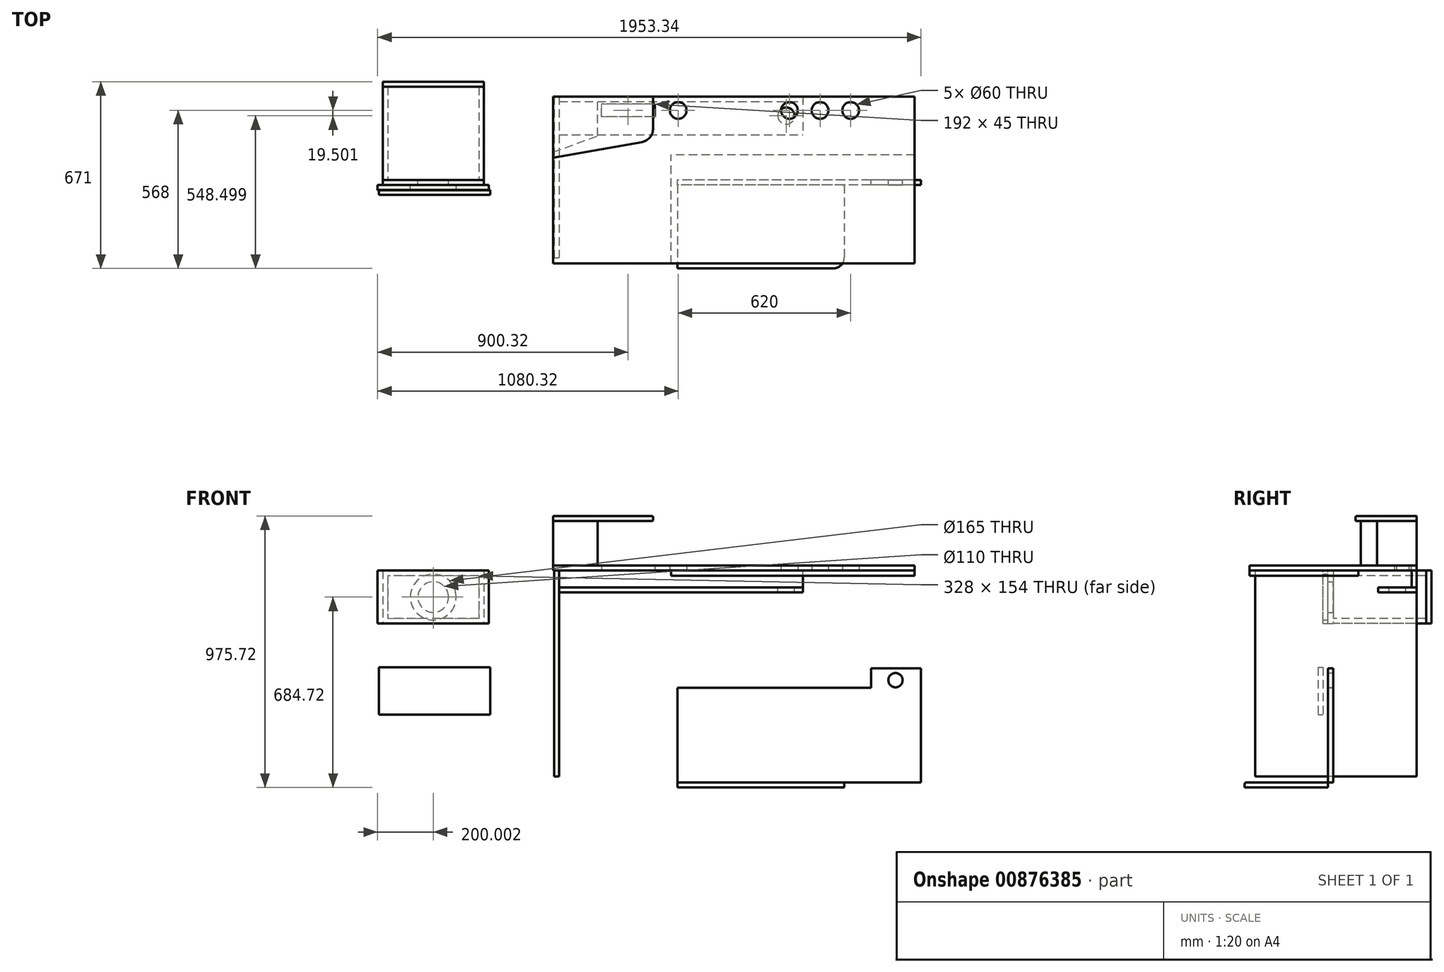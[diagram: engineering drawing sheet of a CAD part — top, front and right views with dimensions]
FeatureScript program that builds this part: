
annotation { "Feature Type Name" : "Feature", "Feature Type Description" : "" }
export const myFeature = defineFeature(function(context is Context, id is Id, definition is map)
    precondition{}
    {
        {
            var Q0;
            Q0=qCreatedBy(makeId("Top.planeOp"),FACE);
            var sketch = newSketch(context, id + "F0", { "sketchPlane" : qUnion([Q0])});
            skLineSegment(sketch, "E0.bottom", {"start": v(650, -300) * mm, "end": v(-650, -300) * mm});
            skLineSegment(sketch, "E0.top", {"start": v(650, 300) * mm, "end": v(-650, 300) * mm});
            skLineSegment(sketch, "E0.left", {"start": v(650, -300) * mm, "end": v(650, 300) * mm});
            skLineSegment(sketch, "E0.right", {"start": v(-650, -300) * mm, "end": v(-650, 300) * mm});
            skPoint(sketch, "E0.middle", {"position": v(0, 0) * mm});
            skLineSegment(sketch, "E1", {"start": v(-650, 250) * mm, "end": v(650, 250) * mm, "construction": true});
            skCircle(sketch, "E2", {"center": v(420, 250) * mm, "radius": 30 * mm});
            skCircle(sketch, "E3.1.0.0", {"center": v(-200, 250) * mm, "radius": 30 * mm});
            skCircle(sketch, "E3.2.0.0", {"center": v(200, 250) * mm, "radius": 30 * mm});
            skCircle(sketch, "E3.3.0.0", {"center": v(310, 250) * mm, "radius": 30 * mm});
            skLineSegment(sketch, "E3.direction1", {"start": v(-200, 250) * mm, "end": v(420, 250) * mm, "construction": true});
            skLineSegment(sketch, "E4.bottom", {"start": v(-284, 227.5) * mm, "end": v(-476, 227.5) * mm});
            skLineSegment(sketch, "E4.top", {"start": v(-284, 272.5) * mm, "end": v(-476, 272.5) * mm});
            skLineSegment(sketch, "E4.left", {"start": v(-284, 227.5) * mm, "end": v(-284, 272.5) * mm});
            skLineSegment(sketch, "E4.right", {"start": v(-476, 227.5) * mm, "end": v(-476, 272.5) * mm});
            skPoint(sketch, "E4.middle", {"position": v(-380, 250) * mm});
            skSolve(sketch);
        }
        {
            var Q0;
            Q0 = qSketchRegion(id + "F0", true);
            extrude(context, id + "F1", {"entities" : qUnion([Q0]), "depth" : 18 * mm, "offsetDistance" : 25 * mm});
        }
        {
            var Q0;
            Q0=makeQuery(id+"F1.opExtrude","CAP_FACE",FACE,{"disambiguationData":[OSD([sQuery(id+"F0.wireOp",EDGE,"E0.bottom"),sQuery(id+"F0.wireOp",EDGE,"E0.top"),sQuery(id+"F0.wireOp",EDGE,"E0.left"),sQuery(id+"F0.wireOp",EDGE,"E0.right")])],"isStart":true});
            var sketch = newSketch(context, id + "F2", { "sketchPlane" : qUnion([Q0])});
            skLineSegment(sketch, "E5.bottom", {"start": v(-627.74, -300) * mm, "end": v(248.26, -300) * mm});
            skLineSegment(sketch, "E5.top", {"start": v(-627.74, -282) * mm, "end": v(248.26, -282) * mm});
            skLineSegment(sketch, "E5.left", {"start": v(-627.74, -300) * mm, "end": v(-627.74, -282) * mm});
            skLineSegment(sketch, "E5.right", {"start": v(248.26, -300) * mm, "end": v(248.26, -282) * mm});
            skSolve(sketch);
        }
        {
            var Q0;
            Q0 = qSketchRegion(id + "F2", true);
            extrude(context, id + "F3", {"entities" : qUnion([Q0]), "depth" : 60 * mm, "offsetDistance" : 25 * mm});
        }
        {
            var Q0;
            Q0=makeQuery(id+"F3.opExtrude","CAP_FACE",FACE,{"disambiguationData":[OSD([sQuery(id+"F2.wireOp",EDGE,"E5.bottom"),sQuery(id+"F2.wireOp",EDGE,"E5.top"),sQuery(id+"F2.wireOp",EDGE,"E5.left"),sQuery(id+"F2.wireOp",EDGE,"E5.right")])],"isStart":false});
            var sketch = newSketch(context, id + "F4", { "sketchPlane" : qUnion([Q0])});
            skLineSegment(sketch, "E6.bottom", {"start": v(-627.74, -300) * mm, "end": v(248.26, -300) * mm});
            skLineSegment(sketch, "E6.top", {"start": v(-627.74, -162) * mm, "end": v(248.26, -162) * mm});
            skLineSegment(sketch, "E6.left", {"start": v(-627.74, -300) * mm, "end": v(-627.74, -162) * mm});
            skLineSegment(sketch, "E6.right", {"start": v(248.26, -300) * mm, "end": v(248.26, -162) * mm});
            skCircle(sketch, "E7", {"center": v(188.26, -230.5) * mm, "radius": 30 * mm});
            skSolve(sketch);
        }
        {
            var Q0;
            Q0 = qSketchRegion(id + "F4", true);
            extrude(context, id + "F5", {"entities" : qUnion([Q0]), "depth" : 18 * mm, "offsetDistance" : 25 * mm});
        }
        {
            var Q0;
            Q0=makeQuery(id+"F3.opExtrude","SWEPT_FACE",FACE,{"disambiguationData":[OSD([sQuery(id+"F2.wireOp",EDGE,"E5.left")])]});
            var sketch = newSketch(context, id + "F6", { "sketchPlane" : qUnion([Q0])});
            skLineSegment(sketch, "E8.bottom", {"start": v(-300, 0) * mm, "end": v(280, 0) * mm});
            skLineSegment(sketch, "E8.top", {"start": v(-300, -740) * mm, "end": v(280, -740) * mm});
            skLineSegment(sketch, "E8.left", {"start": v(-300, 0) * mm, "end": v(-300, -740) * mm});
            skLineSegment(sketch, "E8.right", {"start": v(280, 0) * mm, "end": v(280, -740) * mm});
            skSolve(sketch);
        }
        {
            var Q0;
            Q0 = qSketchRegion(id + "F6", true);
            extrude(context, id + "F7", {"entities" : qUnion([Q0]), "depth" : 18 * mm, "offsetDistance" : 25 * mm});
        }
        {
            var Q0;
            Q0=makeQuery(id+"F1.opExtrude","CAP_FACE",FACE,{"disambiguationData":[OSD([sQuery(id+"F0.wireOp",EDGE,"E0.bottom"),sQuery(id+"F0.wireOp",EDGE,"E0.top"),sQuery(id+"F0.wireOp",EDGE,"E0.left"),sQuery(id+"F0.wireOp",EDGE,"E0.right")])],"isStart":false});
            var sketch = newSketch(context, id + "F8", { "sketchPlane" : qUnion([Q0])});
            skLineSegment(sketch, "E9", {"start": v(-650, 300) * mm, "end": v(-650, 100) * mm});
            skLineSegment(sketch, "E10", {"start": v(-650, 100) * mm, "end": v(-490, 158.24) * mm});
            skLineSegment(sketch, "E11", {"start": v(-490, 158.24) * mm, "end": v(-490, 300) * mm});
            skLineSegment(sketch, "E12", {"start": v(-490, 300) * mm, "end": v(-650, 300) * mm});
            skSolve(sketch);
        }
        {
            var Q0;
            Q0 = qSketchRegion(id + "F8", true);
            extrude(context, id + "F9", {"entities" : qUnion([Q0]), "depth" : 160 * mm, "offsetDistance" : 25 * mm});
        }
        {
            var Q0;
            Q0=makeQuery(id+"F9.opExtrude","CAP_FACE",FACE,{"disambiguationData":[OSD([sQuery(id+"F8.wireOp",EDGE,"E9"),sQuery(id+"F8.wireOp",EDGE,"E10"),sQuery(id+"F8.wireOp",EDGE,"E11"),sQuery(id+"F8.wireOp",EDGE,"E12")])],"isStart":false});
            var sketch = newSketch(context, id + "F10", { "sketchPlane" : qUnion([Q0])});
            skLineSegment(sketch, "E13", {"start": v(-650, 80) * mm, "end": v(-650, 300) * mm});
            skLineSegment(sketch, "E14", {"start": v(-650, 80) * mm, "end": v(-650, 80) * mm});
            skLineSegment(sketch, "E15", {"start": v(-650, 300) * mm, "end": v(-290, 300) * mm});
            skLineSegment(sketch, "E16", {"start": v(-290, 300) * mm, "end": v(-290, 185.43) * mm});
            skLineSegment(sketch, "E17", {"start": v(-331.32, 136.2) * mm, "end": v(-650, 80) * mm});
            skPoint(sketch, "E18.visualSharp", {"position": v(-290, 143.48) * mm});
            skArc(sketch, "E18.filletArc", {"start": v(-331.32, 136.2) * mm, "mid": v(-301.7, 153.3) * mm, "end": v(-290, 185.43) * mm});
            skSolve(sketch);
        }
        {
            var Q0;
            Q0 = qSketchRegion(id + "F10", true);
            extrude(context, id + "F11", {"entities" : qUnion([Q0]), "depth" : 18 * mm, "offsetDistance" : 25 * mm});
        }
        {
            var Q0;
            Q0=makeQuery(id+"F11.opExtrude","CAP_EDGE",EDGE,{"disambiguationData":[OSD([sQuery(id+"F10.wireOp",EDGE,"E17")])],"isStart":false});
            var Q1;
            Q1=makeQuery(id+"F11.opExtrude","CAP_EDGE",EDGE,{"disambiguationData":[OSD([sQuery(id+"F10.wireOp",EDGE,"E18.filletArc")])],"isStart":false});
            var Q2;
            Q2=makeQuery(id+"F11.opExtrude","CAP_EDGE",EDGE,{"disambiguationData":[OSD([sQuery(id+"F10.wireOp",EDGE,"E16")])],"isStart":false});
            var Q3;
            Q3=makeQuery(id+"F11.opExtrude","CAP_EDGE",EDGE,{"disambiguationData":[OSD([sQuery(id+"F10.wireOp",EDGE,"E17")])],"isStart":true});
            var Q4;
            Q4=makeQuery(id+"F11.opExtrude","CAP_EDGE",EDGE,{"disambiguationData":[OSD([sQuery(id+"F10.wireOp",EDGE,"E18.filletArc")])],"isStart":true});
            var Q5;
            Q5=makeQuery(id+"F11.opExtrude","CAP_EDGE",EDGE,{"disambiguationData":[OSD([sQuery(id+"F10.wireOp",EDGE,"E16")])],"isStart":true});
            fillet(context, id + "F12", {"entities" : qUnion([Q0, Q1, Q2, Q3, Q4, Q5]), "radius" : 5 * mm, "tangentPropagation" : true, "allowEdgeOverflow" : false});
        }
        {
            var Q0;
            Q0=qCreatedBy(makeId("Front.planeOp"),FACE);
            var sketch = newSketch(context, id + "F13", { "sketchPlane" : qUnion([Q0])});
            skLineSegment(sketch, "E19.bottom", {"start": v(-1262.32, 0) * mm, "end": v(-898.32, 0) * mm});
            skLineSegment(sketch, "E19.top", {"start": v(-1262.32, -190) * mm, "end": v(-898.32, -190) * mm});
            skLineSegment(sketch, "E19.left", {"start": v(-1262.32, 0) * mm, "end": v(-1262.32, -190) * mm});
            skLineSegment(sketch, "E19.right", {"start": v(-898.32, 0) * mm, "end": v(-898.32, -190) * mm});
            skCircle(sketch, "E20", {"center": v(-1080.32, -95) * mm, "radius": 55 * mm});
            skPoint(sketch, "E20.centerSnap0", {"position": v(-1080.32, -190) * mm});
            skPoint(sketch, "E20.centerSnap1", {"position": v(-1262.32, -95) * mm});
            skSolve(sketch);
        }
        {
            var Q0;
            Q0 = qSketchRegion(id + "F13", true);
            extrude(context, id + "F14", {"entities" : qUnion([Q0]), "depth" : 18 * mm, "offsetDistance" : 25 * mm});
        }
        {
            var Q0;
            Q0=makeQuery(id+"F14.opExtrude","CAP_FACE",FACE,{"disambiguationData":[OSD([sQuery(id+"F13.wireOp",EDGE,"E19.bottom"),sQuery(id+"F13.wireOp",EDGE,"E19.top"),sQuery(id+"F13.wireOp",EDGE,"E19.left"),sQuery(id+"F13.wireOp",EDGE,"E19.right"),sQuery(id+"F13.wireOp",EDGE,"E20")])],"isStart":true});
            var sketch = newSketch(context, id + "F15", { "sketchPlane" : qUnion([Q0])});
            skLineSegment(sketch, "E21.bottom", {"start": v(898.32, 0) * mm, "end": v(1262.32, 0) * mm});
            skLineSegment(sketch, "E21.top", {"start": v(898.32, -190) * mm, "end": v(1262.32, -190) * mm});
            skLineSegment(sketch, "E21.left", {"start": v(898.32, 0) * mm, "end": v(898.32, -190) * mm});
            skLineSegment(sketch, "E21.right", {"start": v(1262.32, 0) * mm, "end": v(1262.32, -190) * mm});
            skLineSegment(sketch, "E22.bottom", {"start": v(916.32, -18) * mm, "end": v(1244.32, -18) * mm});
            skLineSegment(sketch, "E22.top", {"start": v(916.32, -172) * mm, "end": v(1244.32, -172) * mm});
            skLineSegment(sketch, "E22.left", {"start": v(916.32, -18) * mm, "end": v(916.32, -172) * mm});
            skLineSegment(sketch, "E22.right", {"start": v(1244.32, -18) * mm, "end": v(1244.32, -172) * mm});
            skSolve(sketch);
        }
        {
            var Q0;
            Q0 = qSketchRegion(id + "F15", true);
            extrude(context, id + "F16", {"entities" : qUnion([Q0]), "depth" : 335 * mm, "offsetDistance" : 25 * mm});
        }
        {
            var Q0;
            Q0=makeQuery(id+"F14.opExtrude","CAP_FACE",FACE,{"disambiguationData":[OSD([sQuery(id+"F13.wireOp",EDGE,"E19.bottom"),sQuery(id+"F13.wireOp",EDGE,"E19.top"),sQuery(id+"F13.wireOp",EDGE,"E19.left"),sQuery(id+"F13.wireOp",EDGE,"E19.right"),sQuery(id+"F13.wireOp",EDGE,"E20")])],"isStart":false});
            var sketch = newSketch(context, id + "F17", { "sketchPlane" : qUnion([Q0])});
            skLineSegment(sketch, "E23.bottom", {"start": v(-880.32, -190) * mm, "end": v(-1280.32, -190) * mm});
            skLineSegment(sketch, "E23.top", {"start": v(-880.32, 0) * mm, "end": v(-1280.32, 0) * mm});
            skLineSegment(sketch, "E23.left", {"start": v(-880.32, -190) * mm, "end": v(-880.32, 0) * mm});
            skLineSegment(sketch, "E23.right", {"start": v(-1280.32, -190) * mm, "end": v(-1280.32, 0) * mm});
            skPoint(sketch, "E23.middle", {"position": v(-1080.32, -95) * mm});
            skCircle(sketch, "E24", {"center": v(-1080.32, -95) * mm, "radius": 82.5 * mm});
            skSolve(sketch);
        }
        {
            var Q0;
            Q0 = qSketchRegion(id + "F17", true);
            extrude(context, id + "F18", {"entities" : qUnion([Q0]), "depth" : 18 * mm, "offsetDistance" : 25 * mm});
        }
        {
            var Q0;
            Q0=makeQuery(id+"F16.opExtrude","CAP_FACE",FACE,{"disambiguationData":[OSD([sQuery(id+"F15.wireOp",EDGE,"E21.bottom"),sQuery(id+"F15.wireOp",EDGE,"E21.top"),sQuery(id+"F15.wireOp",EDGE,"E21.left"),sQuery(id+"F15.wireOp",EDGE,"E21.right"),sQuery(id+"F15.wireOp",EDGE,"E22.bottom"),sQuery(id+"F15.wireOp",EDGE,"E22.top"),sQuery(id+"F15.wireOp",EDGE,"E22.left"),sQuery(id+"F15.wireOp",EDGE,"E22.right")])],"isStart":false});
            var sketch = newSketch(context, id + "F19", { "sketchPlane" : qUnion([Q0])});
            skLineSegment(sketch, "E25.bottom", {"start": v(898.32, 0) * mm, "end": v(1262.32, 0) * mm});
            skLineSegment(sketch, "E25.top", {"start": v(898.32, -190) * mm, "end": v(1262.32, -190) * mm});
            skLineSegment(sketch, "E25.left", {"start": v(898.32, 0) * mm, "end": v(898.32, -190) * mm});
            skLineSegment(sketch, "E25.right", {"start": v(1262.32, 0) * mm, "end": v(1262.32, -190) * mm});
            skSolve(sketch);
        }
        {
            var Q0;
            Q0 = qSketchRegion(id + "F19", true);
            extrude(context, id + "F20", {"entities" : qUnion([Q0]), "depth" : 18 * mm, "offsetDistance" : 25 * mm});
        }
        {
            var Q0;
            Q0=makeQuery(id+"F1.opExtrude","CAP_FACE",FACE,{"disambiguationData":[OSD([sQuery(id+"F0.wireOp",EDGE,"E0.bottom"),sQuery(id+"F0.wireOp",EDGE,"E0.top"),sQuery(id+"F0.wireOp",EDGE,"E0.left"),sQuery(id+"F0.wireOp",EDGE,"E0.right"),sQuery(id+"F0.wireOp",EDGE,"E2"),sQuery(id+"F0.wireOp",EDGE,"E3.1.0.0"),sQuery(id+"F0.wireOp",EDGE,"E3.2.0.0"),sQuery(id+"F0.wireOp",EDGE,"E3.3.0.0"),sQuery(id+"F0.wireOp",EDGE,"E4.bottom"),sQuery(id+"F0.wireOp",EDGE,"E4.top"),sQuery(id+"F0.wireOp",EDGE,"E4.left"),sQuery(id+"F0.wireOp",EDGE,"E4.right")])],"isStart":true});
            var sketch = newSketch(context, id + "F21", { "sketchPlane" : qUnion([Q0])});
            skLineSegment(sketch, "E26.bottom", {"start": v(650, 300) * mm, "end": v(-226, 300) * mm});
            skLineSegment(sketch, "E26.top", {"start": v(650, -90) * mm, "end": v(-226, -90) * mm});
            skLineSegment(sketch, "E26.left", {"start": v(650, 300) * mm, "end": v(650, -90) * mm});
            skLineSegment(sketch, "E26.right", {"start": v(-226, 300) * mm, "end": v(-226, -90) * mm});
            skSolve(sketch);
        }
        {
            var Q0;
            Q0 = qSketchRegion(id + "F21", true);
            extrude(context, id + "F22", {"entities" : qUnion([Q0]), "depth" : 18 * mm, "offsetDistance" : 25 * mm});
        }
        {
            var Q0;
            Q0=qCreatedBy(makeId("Front.planeOp"),FACE);
            var sketch = newSketch(context, id + "F23", { "sketchPlane" : qUnion([Q0])});
            skLineSegment(sketch, "E27.top", {"start": v(673.02, -761.72) * mm, "end": v(-202.98, -761.72) * mm});
            skLineSegment(sketch, "E27.left", {"start": v(673.02, -351.72) * mm, "end": v(673.02, -761.72) * mm});
            skLineSegment(sketch, "E28", {"start": v(673.02, -351.72) * mm, "end": v(493.02, -351.72) * mm});
            skLineSegment(sketch, "E29", {"start": v(493.02, -351.72) * mm, "end": v(493.02, -421.72) * mm});
            skLineSegment(sketch, "E30", {"start": v(493.02, -421.72) * mm, "end": v(-202.98, -421.72) * mm});
            skLineSegment(sketch, "E31", {"start": v(-202.98, -421.72) * mm, "end": v(-202.98, -761.72) * mm});
            skCircle(sketch, "E32", {"center": v(581.1, -393.66) * mm, "radius": 25.73 * mm});
            skSolve(sketch);
        }
        {
            var Q0;
            Q0 = qSketchRegion(id + "F23", true);
            extrude(context, id + "F24", {"entities" : qUnion([Q0]), "depth" : 18 * mm, "offsetDistance" : 25 * mm});
        }
        {
            var Q0;
            Q0=makeQuery(id+"F24.opExtrude","SWEPT_FACE",FACE,{"disambiguationData":[OSD([sQuery(id+"F23.wireOp",EDGE,"E27.top")])]});
            var sketch = newSketch(context, id + "F25", { "sketchPlane" : qUnion([Q0])});
            skLineSegment(sketch, "E33.bottom", {"start": v(-202.98, 18) * mm, "end": v(397.02, 18) * mm});
            skLineSegment(sketch, "E33.top", {"start": v(-202.98, 318) * mm, "end": v(357.02, 318) * mm});
            skLineSegment(sketch, "E33.left", {"start": v(-202.98, 18) * mm, "end": v(-202.98, 318) * mm});
            skLineSegment(sketch, "E33.right", {"start": v(397.02, 18) * mm, "end": v(397.02, 278) * mm});
            skPoint(sketch, "E34.visualSharp", {"position": v(397.02, 318) * mm});
            skArc(sketch, "E34.filletArc", {"start": v(397.02, 278) * mm, "mid": v(385.3, 306.28) * mm, "end": v(357.02, 318) * mm});
            skSolve(sketch);
        }
        {
            var Q0;
            Q0 = qSketchRegion(id + "F25", true);
            extrude(context, id + "F26", {"entities" : qUnion([Q0]), "depth" : 18 * mm, "offsetDistance" : 25 * mm});
        }
        {
            var Q0;
            Q0=makeQuery(id+"F26.opExtrude","CAP_EDGE",EDGE,{"disambiguationData":[OSD([sQuery(id+"F25.wireOp",EDGE,"E33.top")])],"isStart":true});
            var Q1;
            Q1=makeQuery(id+"F26.opExtrude","CAP_EDGE",EDGE,{"disambiguationData":[OSD([sQuery(id+"F25.wireOp",EDGE,"E34.filletArc")])],"isStart":true});
            var Q2;
            Q2=makeQuery(id+"F26.opExtrude","CAP_EDGE",EDGE,{"disambiguationData":[OSD([sQuery(id+"F25.wireOp",EDGE,"E33.right")])],"isStart":true});
            fillet(context, id + "F27", {"entities" : qUnion([Q0, Q1, Q2]), "radius" : 5 * mm, "tangentPropagation" : true, "allowEdgeOverflow" : false});
        }
        {
            var Q0;
            Q0=makeQuery(id+"F18.opExtrude","CAP_FACE",FACE,{"disambiguationData":[OSD([sQuery(id+"F17.wireOp",EDGE,"E23.bottom"),sQuery(id+"F17.wireOp",EDGE,"E23.top"),sQuery(id+"F17.wireOp",EDGE,"E23.left"),sQuery(id+"F17.wireOp",EDGE,"E23.right"),sQuery(id+"F17.wireOp",EDGE,"E24")])],"isStart":false});
            var sketch = newSketch(context, id + "F28", { "sketchPlane" : qUnion([Q0])});
            skLineSegment(sketch, "E35.bottom", {"start": v(-1276.2, -347.69) * mm, "end": v(-876.2, -347.69) * mm});
            skLineSegment(sketch, "E35.top", {"start": v(-1276.2, -517.69) * mm, "end": v(-876.2, -517.69) * mm});
            skLineSegment(sketch, "E35.left", {"start": v(-1276.2, -347.69) * mm, "end": v(-1276.2, -517.69) * mm});
            skLineSegment(sketch, "E35.right", {"start": v(-876.2, -347.69) * mm, "end": v(-876.2, -517.69) * mm});
            skSolve(sketch);
        }
        {
            var Q0;
            Q0 = qSketchRegion(id + "F28", true);
            extrude(context, id + "F29", {"entities" : qUnion([Q0]), "depth" : 18 * mm, "offsetDistance" : 25 * mm});
        }
        {
            var Q0;
            Q0=makeQuery(id+"F18.opExtrude","CAP_FACE",FACE,{"disambiguationData":[OSD([sQuery(id+"F17.wireOp",EDGE,"E23.bottom"),sQuery(id+"F17.wireOp",EDGE,"E23.top"),sQuery(id+"F17.wireOp",EDGE,"E23.left"),sQuery(id+"F17.wireOp",EDGE,"E23.right"),sQuery(id+"F17.wireOp",EDGE,"E24")])],"isStart":false});
            var sketch = newSketch(context, id + "F30", { "sketchPlane" : qUnion([Q0])});
            skLineSegment(sketch, "E36.bottom", {"start": v(-880.32, -190) * mm, "end": v(-1280.32, -190) * mm});
            skLineSegment(sketch, "E36.top", {"start": v(-880.32, 0) * mm, "end": v(-1280.32, 0) * mm});
            skLineSegment(sketch, "E36.left", {"start": v(-880.32, -190) * mm, "end": v(-880.32, 0) * mm});
            skLineSegment(sketch, "E36.right", {"start": v(-1280.32, -190) * mm, "end": v(-1280.32, 0) * mm});
            skSolve(sketch);
        }
        {
            var Q0;
            Q0 = qSketchRegion(id + "F30", true);
            extrude(context, id + "F31", {"entities" : qUnion([Q0]), "depth" : 1 * mm, "offsetDistance" : 25 * mm});
        }
    });
